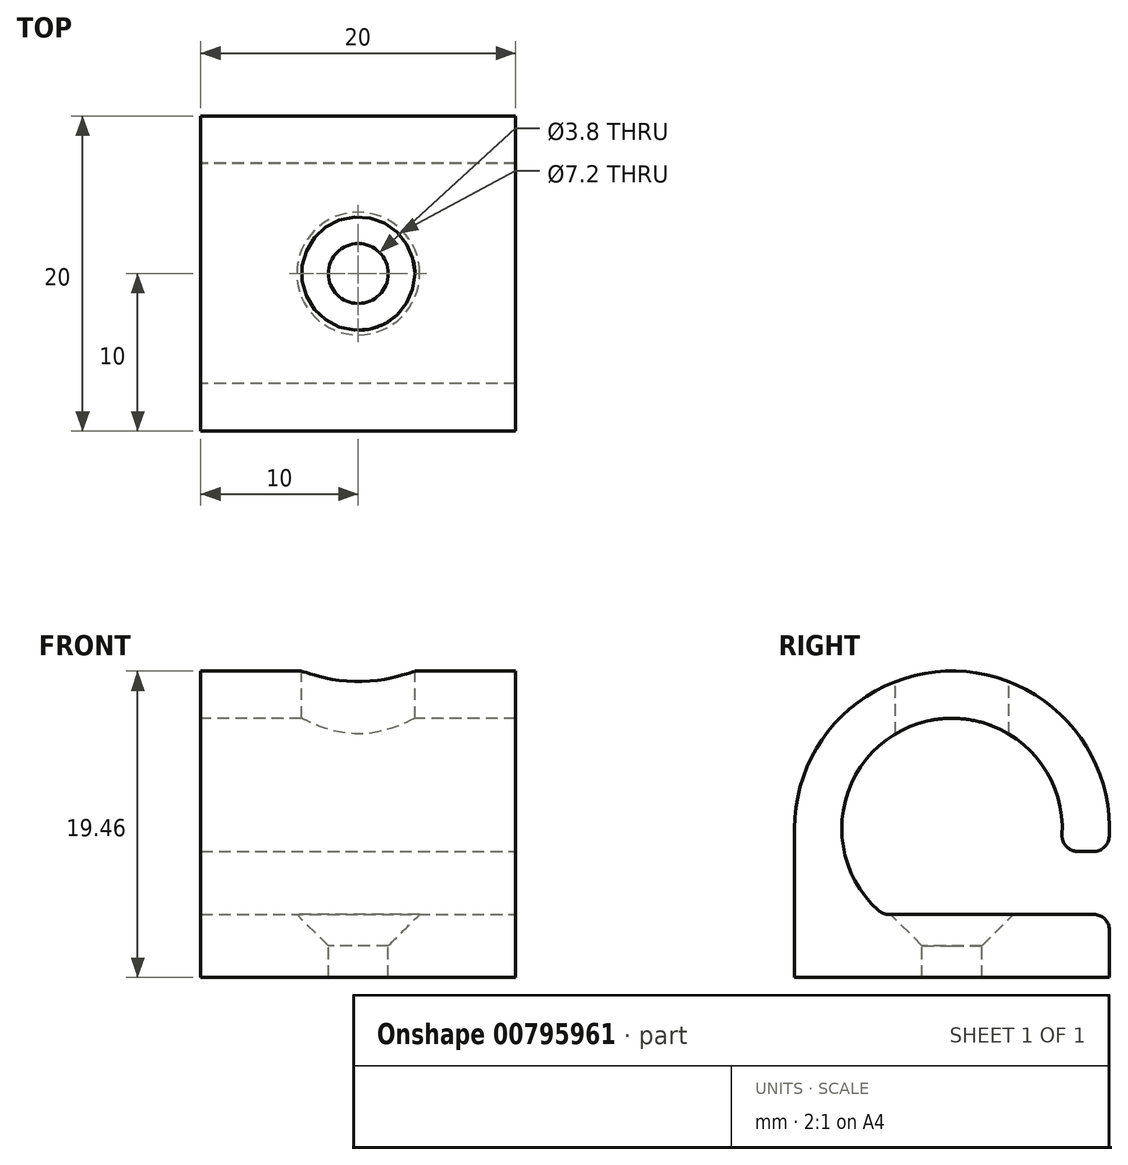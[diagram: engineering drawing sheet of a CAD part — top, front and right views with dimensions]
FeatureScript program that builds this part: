
annotation { "Feature Type Name" : "Feature", "Feature Type Description" : "" }
export const myFeature = defineFeature(function(context is Context, id is Id, definition is map)
    precondition{}
    {
        {
            var Q0;
            Q0=qCreatedBy(makeId("Top.planeOp"),FACE);
            var sketch = newSketch(context, id + "F0", { "sketchPlane" : qUnion([Q0])});
            skLineSegment(sketch, "E0.bottom", {"start": v(-10, 10) * mm, "end": v(10, 10) * mm});
            skLineSegment(sketch, "E0.top", {"start": v(-10, -10) * mm, "end": v(10, -10) * mm});
            skLineSegment(sketch, "E0.left", {"start": v(-10, 10) * mm, "end": v(-10, -10) * mm});
            skLineSegment(sketch, "E0.right", {"start": v(10, 10) * mm, "end": v(10, -10) * mm});
            skSolve(sketch);
        }
        {
            var Q0;
            Q0 = qSketchRegion(id + "F0", true);
            extrude(context, id + "F1", {"entities" : qUnion([Q0]), "endBound" : BoundingType.SYMMETRIC, "depth" : 4 * mm, "offsetDistance" : 25 * mm});
        }
        {
            var Q0;
            Q0=qCreatedBy(makeId("Right.planeOp"),FACE);
            var sketch = newSketch(context, id + "F2", { "sketchPlane" : qUnion([Q0])});
            skArc(sketch, "E1", {"start": v(6.66, 0) * mm, "mid": v(4.09, 16.59) * mm, "end": v(-10, 7.46) * mm});
            skLineSegment(sketch, "E2", {"start": v(6.66, 0) * mm, "end": v(-6.66, 0) * mm});
            skCircle(sketch, "E3", {"center": v(0, 7.46) * mm, "radius": 7 * mm});
            skLineSegment(sketch, "E4", {"start": v(0, 7.46) * mm, "end": v(-16.58, 7.46) * mm, "construction": true});
            skLineSegment(sketch, "E5", {"start": v(-10, 7.46) * mm, "end": v(-10, 0) * mm});
            skLineSegment(sketch, "E6", {"start": v(-10, 0) * mm, "end": v(-6.66, 0) * mm});
            skLineSegment(sketch, "E7", {"start": v(4.38, 2) * mm, "end": v(-4.38, 2) * mm});
            skLineSegment(sketch, "E8", {"start": v(6.66, 0) * mm, "end": v(0, 0) * mm});
            skSolve(sketch);
        }
        {
            var Q0;
            Q0 = qSketchRegion(id + "F2", true);
            extrude(context, id + "F3", {"entities" : qUnion([Q0]), "operationType" : NewBodyOperationType.ADD, "endBound" : BoundingType.SYMMETRIC, "depth" : 20 * mm, "offsetDistance" : 25 * mm});
        }
        {
            var Q0;
            Q0=qCreatedBy(makeId("Right.planeOp"),FACE);
            var sketch = newSketch(context, id + "F4", { "sketchPlane" : qUnion([Q0])});
            skLineSegment(sketch, "E9.bottom", {"start": v(12.68, 6) * mm, "end": v(2.68, 6) * mm});
            skLineSegment(sketch, "E9.top", {"start": v(12.68, 2) * mm, "end": v(2.68, 2) * mm});
            skLineSegment(sketch, "E9.left", {"start": v(12.68, 6) * mm, "end": v(12.68, 2) * mm});
            skLineSegment(sketch, "E9.right", {"start": v(2.68, 6) * mm, "end": v(2.68, 2) * mm});
            skSolve(sketch);
        }
        {
            var Q0;
            Q0 = qSketchRegion(id + "F4", true);
            extrude(context, id + "F5", {"entities" : qUnion([Q0]), "operationType" : NewBodyOperationType.REMOVE, "endBound" : BoundingType.SYMMETRIC, "oppositeDirection" : true, "depth" : 20 * mm, "offsetDistance" : 25 * mm});
        }
        {
            var Q0;
            Q0=makeQuery(id+"F1.opExtrude","CAP_EDGE",EDGE,{"disambiguationData":[OSD([sQuery(id+"F0.wireOp",EDGE,"E0.bottom")])],"isStart":false});
            var Q1;
            Q1=makeQuery(id+"F5.boolean.opBoolean","INTERSECT",EDGE,{"derivedFrom":[makeQuery(id+"F3.opExtrude","SWEPT_FACE",FACE,{"disambiguationData":[OSD([sQuery(id+"F2.wireOp",EDGE,"E1")])]}),makeQuery(id+"F5.opExtrude","SWEPT_FACE",FACE,{"disambiguationData":[OSD([sQuery(id+"F4.wireOp",EDGE,"E9.bottom")])]})]});
            var Q2;
            Q2=makeQuery(id+"F5.boolean.opBoolean","INTERSECT",EDGE,{"derivedFrom":[makeQuery(id+"F3.opExtrude","SWEPT_FACE",FACE,{"disambiguationData":[OSD([sQuery(id+"F2.wireOp",EDGE,"E3")])]}),makeQuery(id+"F5.opExtrude","SWEPT_FACE",FACE,{"disambiguationData":[OSD([sQuery(id+"F4.wireOp",EDGE,"E9.bottom")])]})]});
            var Q3;
            Q3=makeQuery(id+"F3.boolean.opBoolean","INTERSECT",EDGE,{"disambiguationData":[OD(0.0)],"derivedFrom":[makeQuery(id+"F1.opExtrude","CAP_FACE",FACE,{"disambiguationData":[OSD([sQuery(id+"F0.wireOp",EDGE,"E0.bottom"),sQuery(id+"F0.wireOp",EDGE,"E0.top"),sQuery(id+"F0.wireOp",EDGE,"E0.left"),sQuery(id+"F0.wireOp",EDGE,"E0.right")])],"isStart":false}),makeQuery(id+"F3.opExtrude","SWEPT_FACE",FACE,{"disambiguationData":[OSD([sQuery(id+"F2.wireOp",EDGE,"E3")])]})]});
            fillet(context, id + "F6", {"entities" : qUnion([Q0, Q1, Q2, Q3]), "radius" : 1 * mm, "tangentPropagation" : true, "allowEdgeOverflow" : false});
        }
        {
            var Q0;
            Q0=makeQuery(id+"F1.opExtrude","CAP_FACE",FACE,{"disambiguationData":[OSD([sQuery(id+"F0.wireOp",EDGE,"E0.bottom"),sQuery(id+"F0.wireOp",EDGE,"E0.top"),sQuery(id+"F0.wireOp",EDGE,"E0.left"),sQuery(id+"F0.wireOp",EDGE,"E0.right")])],"isStart":true});
            cPlane(context, id + "F7", {"entities" : qUnion([Q0]), "cplaneType" : CPlaneType.OFFSET, "offset" : 22.2 * mm, "oppositeDirection" : true, "width" : 150 * mm, "height" : 150 * mm});
        }
        {
            var Q0;
            Q0=qCreatedBy(id+"F7.planeOp",FACE);
            var sketch = newSketch(context, id + "F8", { "sketchPlane" : qUnion([Q0])});
            skCircle(sketch, "E10", {"center": v(0, 0) * mm, "radius": 1.9 * mm});
            skCircle(sketch, "E11", {"center": v(0, 0) * mm, "radius": 3.6 * mm});
            skSolve(sketch);
        }
        {
            var Q0;
            Q0=makeQuery(id+"F8.imprint","IMPRINT",FACE,{"disambiguationData":[TD([[makeQuery(id+"F8.imprint","IMPRINT",EDGE,{"derivedFrom":sQuery(id+"F8.wireOp",EDGE,"E10")}),1.0]])]});
            extrude(context, id + "F9", {"entities" : qUnion([Q0]), "operationType" : NewBodyOperationType.REMOVE, "depth" : 25 * mm, "offsetDistance" : 25 * mm});
        }
        {
            var Q0;
            Q0=makeQuery(id+"F8.imprint","IMPRINT",FACE,{"disambiguationData":[TD([[makeQuery(id+"F8.imprint","IMPRINT",EDGE,{"derivedFrom":sQuery(id+"F8.wireOp",EDGE,"E10")}),-1.0]])]});
            var Q1;
            Q1 = qConstructionFilter(qBodyType(qCreatedBy(id + "F8" ,EDGE), BodyType.WIRE), ConstructionObject.NO);
            extrude(context, id + "F10", {"entities" : qUnion([Q0]), "operationType" : NewBodyOperationType.REMOVE, "surfaceEntities" : qUnion([Q1]), "depth" : 15 * mm, "offsetDistance" : 25 * mm});
        }
        {
            var Q0;
            {var subQ3=sQuery(id+"F2.wireOp",EDGE,"E3");var subQ8=sQuery(id+"F0.wireOp",EDGE,"E0.right");var subQ10=sQuery(id+"F0.wireOp",EDGE,"E0.left");var subQ12=sQuery(id+"F0.wireOp",EDGE,"E0.bottom");var subQ13=makeQuery(id+"F1.opExtrude","CAP_FACE",FACE,{"disambiguationData":[OSD([subQ12,sQuery(id+"F0.wireOp",EDGE,"E0.top"),subQ10,subQ8])],"isStart":false});Q0=makeQuery(id+"F9.boolean.opBoolean","INTERSECT",EDGE,{"derivedFrom":[makeQuery(id+"F5.boolean.opBoolean","MERGE",FACE,{"derivedFrom":[makeQuery(id+"F3.boolean.opBoolean","SPLIT",FACE,{"disambiguationData":[TD([makeQuery(id+"F1.opExtrude","SWEPT_FACE",FACE,{"disambiguationData":[OSD([subQ12])]})])],"derivedFrom":subQ13}),makeQuery(id+"F3.boolean.opBoolean","SPLIT",FACE,{"disambiguationData":[TD([makeQuery(id+"F3.opExtrude","SWEPT_FACE",FACE,{"disambiguationData":[OSD([subQ3])]})])],"derivedFrom":subQ13})],"fromTools":[makeQuery(id+"F5.opExtrude","SWEPT_FACE",FACE,{"disambiguationData":[OSD([sQuery(id+"F4.wireOp",EDGE,"E9.top")])]})]}),makeQuery(id+"F9.opExtrude","SWEPT_FACE",FACE,{"disambiguationData":[OSD([sQuery(id+"F8.wireOp",EDGE,"E10")])]})]});}
            chamfer(context, id + "F11", {"entities" : qUnion([Q0]), "width" : 2 * mm, "tangentPropagation" : true});
        }
    });
